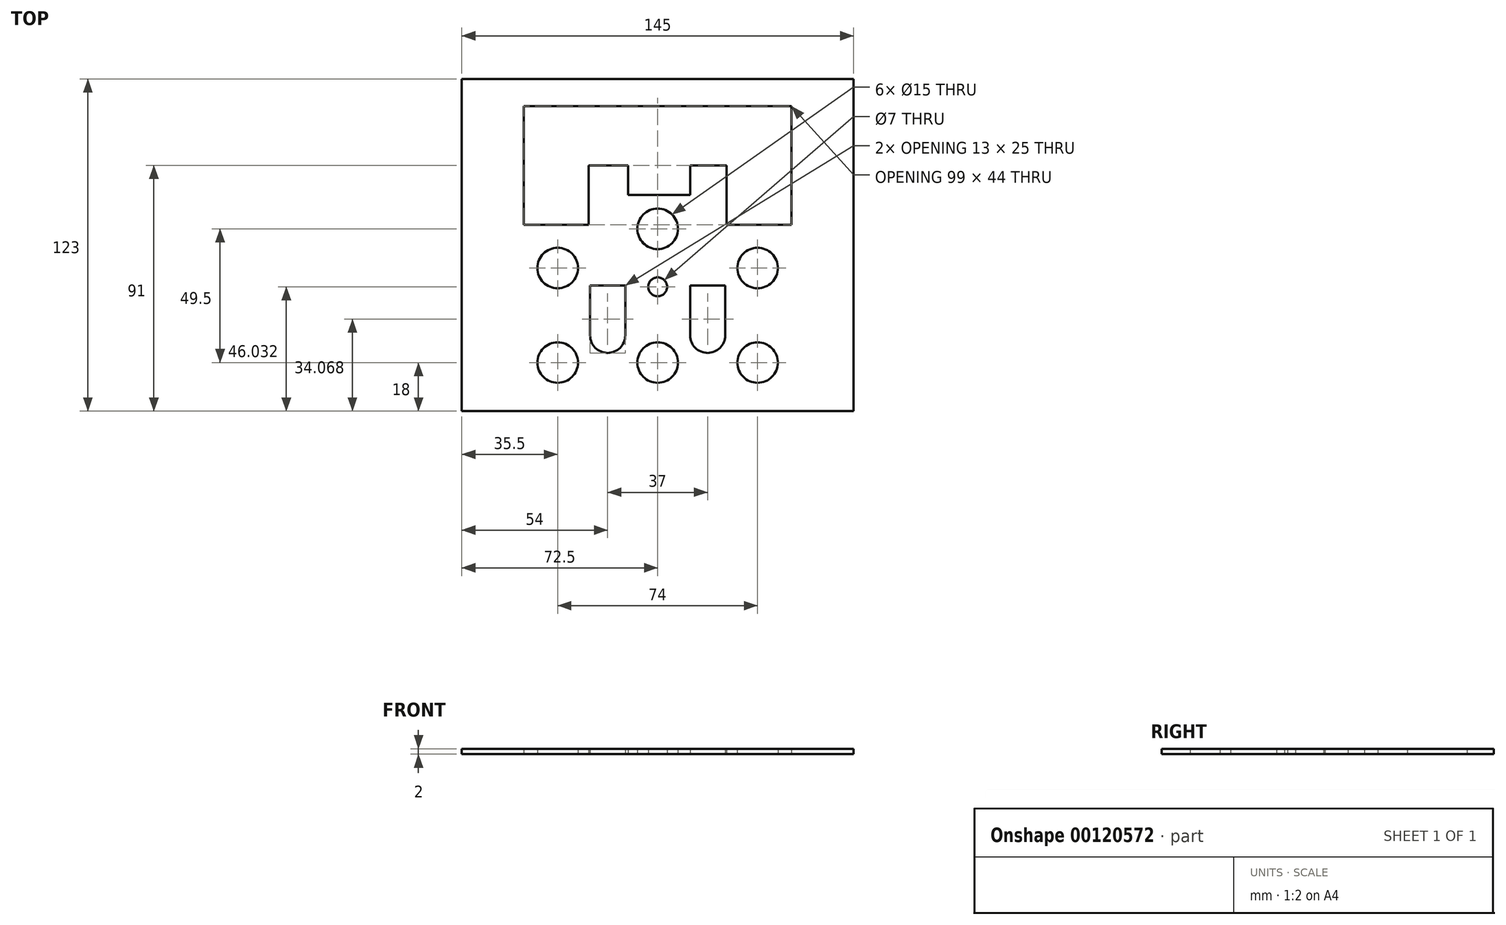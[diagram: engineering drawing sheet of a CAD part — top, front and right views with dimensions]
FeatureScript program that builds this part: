
annotation { "Feature Type Name" : "Feature", "Feature Type Description" : "" }
export const myFeature = defineFeature(function(context is Context, id is Id, definition is map)
    precondition{}
    {
        {
            var Q0;
            Q0=qCreatedBy(makeId("Top.planeOp"),FACE);
            var sketch = newSketch(context, id + "F0", { "sketchPlane" : qUnion([Q0])});
            skLineSegment(sketch, "E0.bottom", {"start": v(0, 0) * mm, "end": v(145, 0) * mm});
            skLineSegment(sketch, "E0.left", {"start": v(0, 0) * mm, "end": v(0, -123) * mm});
            skLineSegment(sketch, "E0.right", {"start": v(145, 0) * mm, "end": v(145, -123) * mm});
            skLineSegment(sketch, "E1", {"start": v(0, -123) * mm, "end": v(145, -123) * mm});
            skLineSegment(sketch, "E2", {"start": v(23, -10) * mm, "end": v(23, -54) * mm});
            skLineSegment(sketch, "E3", {"start": v(23, -54) * mm, "end": v(47, -54) * mm});
            skLineSegment(sketch, "E4", {"start": v(47, -54) * mm, "end": v(47, -32) * mm});
            skLineSegment(sketch, "E5", {"start": v(47, -32) * mm, "end": v(98, -32) * mm});
            skLineSegment(sketch, "E6", {"start": v(98, -32) * mm, "end": v(98, -54) * mm});
            skLineSegment(sketch, "E7", {"start": v(122, -54) * mm, "end": v(122, -10) * mm});
            skLineSegment(sketch, "E8", {"start": v(122, -10) * mm, "end": v(23, -10) * mm});
            skLineSegment(sketch, "E9", {"start": v(98, -54) * mm, "end": v(122, -54) * mm});
            skLineSegment(sketch, "E10.bottom", {"start": v(49, -10) * mm, "end": v(71, -10) * mm, "construction": true});
            skLineSegment(sketch, "E10.top", {"start": v(49, -20) * mm, "end": v(71, -20) * mm, "construction": true});
            skLineSegment(sketch, "E10.left", {"start": v(49, -10) * mm, "end": v(49, -20) * mm, "construction": true});
            skLineSegment(sketch, "E10.right", {"start": v(71, -10) * mm, "end": v(71, -20) * mm, "construction": true});
            skLineSegment(sketch, "E11.bottom", {"start": v(74, -10) * mm, "end": v(96, -10) * mm, "construction": true});
            skLineSegment(sketch, "E11.top", {"start": v(74, -20) * mm, "end": v(96, -20) * mm, "construction": true});
            skLineSegment(sketch, "E11.left", {"start": v(74, -10) * mm, "end": v(74, -20) * mm, "construction": true});
            skLineSegment(sketch, "E11.right", {"start": v(96, -10) * mm, "end": v(96, -20) * mm, "construction": true});
            skLineSegment(sketch, "E12.bottom", {"start": v(99, -10) * mm, "end": v(121, -10) * mm, "construction": true});
            skLineSegment(sketch, "E12.top", {"start": v(99, -20) * mm, "end": v(121, -20) * mm, "construction": true});
            skLineSegment(sketch, "E12.left", {"start": v(99, -10) * mm, "end": v(99, -20) * mm, "construction": true});
            skLineSegment(sketch, "E12.right", {"start": v(121, -10) * mm, "end": v(121, -20) * mm, "construction": true});
            skCircle(sketch, "E13", {"center": v(72.5, -55.5) * mm, "radius": 7.5 * mm});
            skCircle(sketch, "E14", {"center": v(35.5, -70) * mm, "radius": 7.5 * mm});
            skLineSegment(sketch, "E15.bottom", {"start": v(61.5, -32) * mm, "end": v(84.5, -32) * mm});
            skLineSegment(sketch, "E15.top", {"start": v(61.5, -43) * mm, "end": v(84.5, -43) * mm});
            skLineSegment(sketch, "E15.left", {"start": v(61.5, -32) * mm, "end": v(61.5, -43) * mm});
            skLineSegment(sketch, "E15.right", {"start": v(84.5, -32) * mm, "end": v(84.5, -43) * mm});
            skLineSegment(sketch, "E16.bottom", {"start": v(24, -10) * mm, "end": v(46, -10) * mm, "construction": true});
            skLineSegment(sketch, "E16.top", {"start": v(24, -20) * mm, "end": v(46, -20) * mm, "construction": true});
            skLineSegment(sketch, "E16.left", {"start": v(24, -10) * mm, "end": v(24, -20) * mm});
            skLineSegment(sketch, "E16.right", {"start": v(46, -10) * mm, "end": v(46, -20) * mm, "construction": true});
            skCircle(sketch, "E17", {"center": v(109.5, -105) * mm, "radius": 7.5 * mm});
            skCircle(sketch, "E18", {"center": v(109.5, -70) * mm, "radius": 7.5 * mm});
            skCircle(sketch, "E19", {"center": v(35.5, -105) * mm, "radius": 7.5 * mm});
            skLineSegment(sketch, "E20.bottom", {"start": v(24, -21) * mm, "end": v(46, -21) * mm, "construction": true});
            skLineSegment(sketch, "E20.top", {"start": v(24, -31) * mm, "end": v(46, -31) * mm, "construction": true});
            skLineSegment(sketch, "E20.left", {"start": v(24, -21) * mm, "end": v(24, -31) * mm, "construction": true});
            skLineSegment(sketch, "E20.right", {"start": v(46, -21) * mm, "end": v(46, -31) * mm, "construction": true});
            skLineSegment(sketch, "E21.bottom", {"start": v(24, -32) * mm, "end": v(46, -32) * mm, "construction": true});
            skLineSegment(sketch, "E21.top", {"start": v(24, -42) * mm, "end": v(46, -42) * mm, "construction": true});
            skLineSegment(sketch, "E21.left", {"start": v(24, -32) * mm, "end": v(24, -42) * mm, "construction": true});
            skLineSegment(sketch, "E21.right", {"start": v(46, -32) * mm, "end": v(46, -42) * mm, "construction": true});
            skLineSegment(sketch, "E22.bottom", {"start": v(24, -43) * mm, "end": v(46, -43) * mm, "construction": true});
            skLineSegment(sketch, "E22.top", {"start": v(24, -53) * mm, "end": v(46, -53) * mm, "construction": true});
            skLineSegment(sketch, "E22.left", {"start": v(24, -43) * mm, "end": v(24, -53) * mm, "construction": true});
            skLineSegment(sketch, "E22.right", {"start": v(46, -43) * mm, "end": v(46, -53) * mm, "construction": true});
            skPoint(sketch, "E23", {"position": v(47, -43) * mm});
            skCircle(sketch, "E24", {"center": v(72.5, -105) * mm, "radius": 7.5 * mm});
            skCircle(sketch, "E25", {"center": v(72.5, -76.97) * mm, "radius": 6.5 * mm, "construction": true});
            skCircle(sketch, "E26", {"center": v(72.5, -76.97) * mm, "radius": 3.5 * mm});
            skLineSegment(sketch, "E27.bottom", {"start": v(47.5, -76.43) * mm, "end": v(60.5, -76.43) * mm});
            skLineSegment(sketch, "E27.top", {"start": v(54, -101.43) * mm, "end": v(54, -101.43) * mm});
            skLineSegment(sketch, "E27.left", {"start": v(47.5, -76.43) * mm, "end": v(47.5, -94.93) * mm});
            skLineSegment(sketch, "E27.right", {"start": v(60.5, -76.43) * mm, "end": v(60.5, -94.93) * mm});
            skPoint(sketch, "E28.visualSharp", {"position": v(47.5, -101.43) * mm});
            skArc(sketch, "E28.filletArc", {"start": v(47.5, -94.93) * mm, "mid": v(49.4, -99.53) * mm, "end": v(54, -101.43) * mm});
            skPoint(sketch, "E29.visualSharp", {"position": v(60.5, -101.43) * mm});
            skArc(sketch, "E29.filletArc", {"start": v(54, -101.43) * mm, "mid": v(58.6, -99.53) * mm, "end": v(60.5, -94.93) * mm});
            skLineSegment(sketch, "E30.bottom", {"start": v(84.5, -76.43) * mm, "end": v(97.5, -76.43) * mm});
            skLineSegment(sketch, "E30.top", {"start": v(91, -101.43) * mm, "end": v(91, -101.43) * mm});
            skLineSegment(sketch, "E30.left", {"start": v(84.5, -76.43) * mm, "end": v(84.5, -94.93) * mm});
            skLineSegment(sketch, "E30.right", {"start": v(97.5, -76.43) * mm, "end": v(97.5, -94.93) * mm});
            skPoint(sketch, "E31.visualSharp", {"position": v(84.5, -101.43) * mm});
            skArc(sketch, "E31.filletArc", {"start": v(84.5, -94.93) * mm, "mid": v(86.4, -99.53) * mm, "end": v(91, -101.43) * mm});
            skPoint(sketch, "E32.visualSharp", {"position": v(97.5, -101.43) * mm});
            skArc(sketch, "E32.filletArc", {"start": v(91, -101.43) * mm, "mid": v(95.6, -99.53) * mm, "end": v(97.5, -94.93) * mm});
            skLineSegment(sketch, "E33.bottom", {"start": v(49, -21) * mm, "end": v(71, -21) * mm, "construction": true});
            skLineSegment(sketch, "E33.top", {"start": v(49, -31) * mm, "end": v(71, -31) * mm, "construction": true});
            skLineSegment(sketch, "E33.left", {"start": v(49, -21) * mm, "end": v(49, -31) * mm, "construction": true});
            skLineSegment(sketch, "E33.right", {"start": v(71, -21) * mm, "end": v(71, -31) * mm, "construction": true});
            skLineSegment(sketch, "E34.bottom", {"start": v(74, -21) * mm, "end": v(96, -21) * mm, "construction": true});
            skLineSegment(sketch, "E34.top", {"start": v(74, -31) * mm, "end": v(96, -31) * mm, "construction": true});
            skLineSegment(sketch, "E34.left", {"start": v(74, -21) * mm, "end": v(74, -31) * mm, "construction": true});
            skLineSegment(sketch, "E34.right", {"start": v(96, -21) * mm, "end": v(96, -31) * mm, "construction": true});
            skLineSegment(sketch, "E35.bottom", {"start": v(99, -21) * mm, "end": v(121, -21) * mm, "construction": true});
            skLineSegment(sketch, "E35.top", {"start": v(99, -31) * mm, "end": v(121, -31) * mm, "construction": true});
            skLineSegment(sketch, "E35.left", {"start": v(99, -21) * mm, "end": v(99, -31) * mm, "construction": true});
            skLineSegment(sketch, "E35.right", {"start": v(121, -21) * mm, "end": v(121, -31) * mm, "construction": true});
            skLineSegment(sketch, "E36.bottom", {"start": v(99, -32) * mm, "end": v(121, -32) * mm, "construction": true});
            skLineSegment(sketch, "E36.top", {"start": v(99, -42) * mm, "end": v(121, -42) * mm, "construction": true});
            skLineSegment(sketch, "E36.left", {"start": v(99, -32) * mm, "end": v(99, -42) * mm, "construction": true});
            skLineSegment(sketch, "E36.right", {"start": v(121, -32) * mm, "end": v(121, -42) * mm, "construction": true});
            skSolve(sketch);
        }
        {
            var Q0;
            Q0 = qSketchRegion(id + "F0", true);
            extrude(context, id + "F1", {"entities" : qUnion([Q0]), "depth" : 2 * mm});
        }
    });
